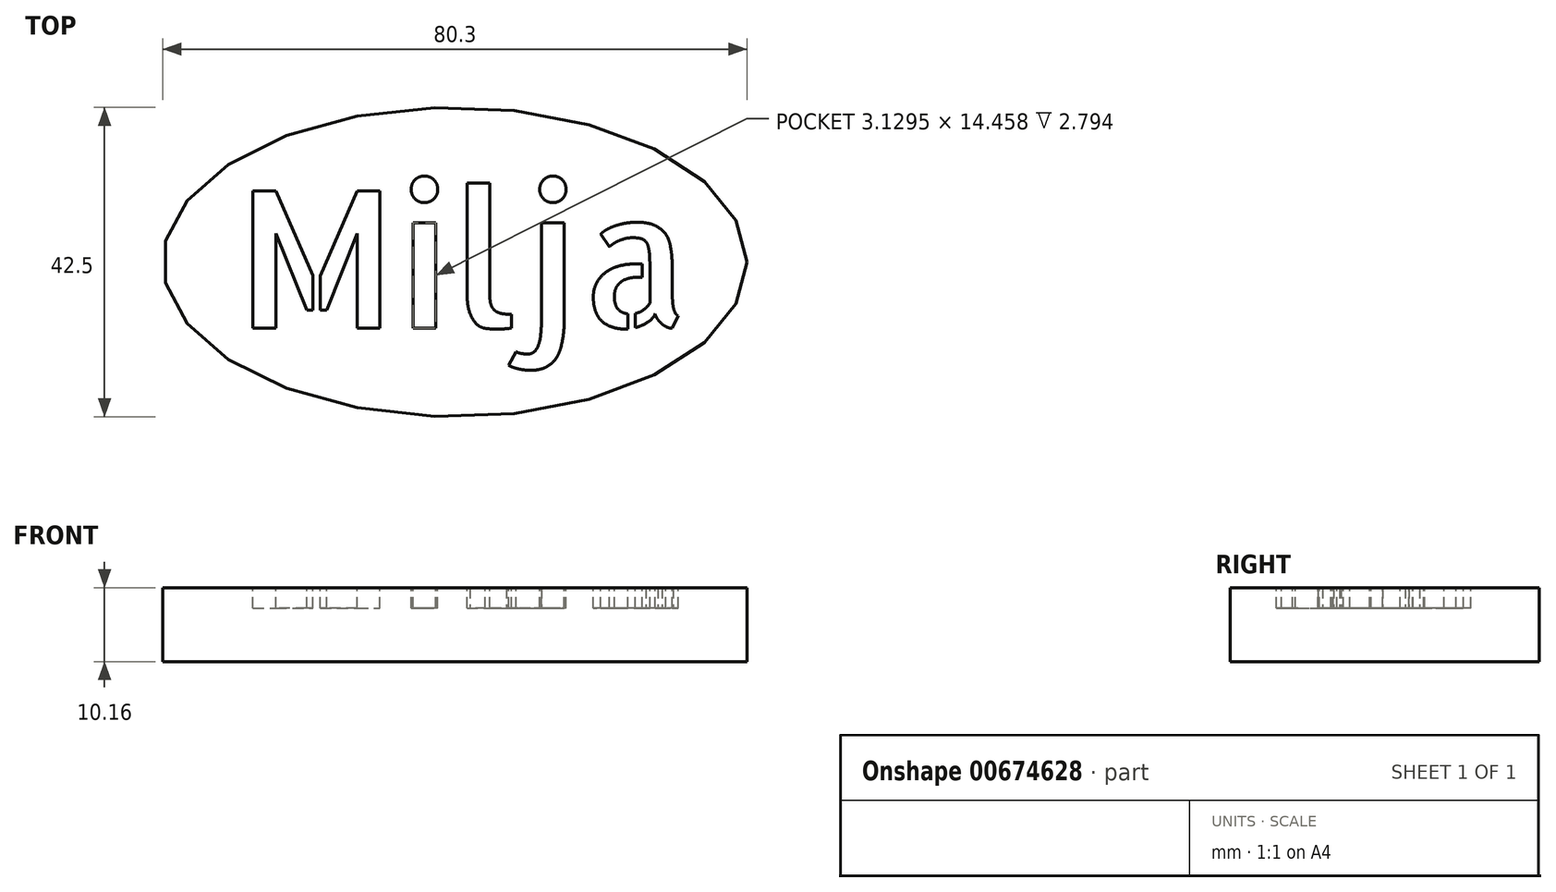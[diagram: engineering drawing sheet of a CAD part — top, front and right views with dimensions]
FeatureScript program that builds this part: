
annotation { "Feature Type Name" : "Feature", "Feature Type Description" : "" }
export const myFeature = defineFeature(function(context is Context, id is Id, definition is map)
    precondition{}
    {
        {
            var Q0;
            Q0=qCreatedBy(makeId("Top.planeOp"),FACE);
            var sketch = newSketch(context, id + "F0", { "sketchPlane" : qUnion([Q0])});
            skEllipse(sketch, "E0", {"center": v(0, 0) * mm, "majorRadius": 40.15 * mm, "minorRadius": 21.25 * mm, "majorAxis": v(1, 0)});
            skSolve(sketch);
        }
        {
            var Q0;
            Q0=makeQuery(id+"F0.imprint","IMPRINT",FACE,{"disambiguationData":[TD([[makeQuery(id+"F0.imprint","IMPRINT",EDGE,{"derivedFrom":sQuery(id+"F0.wireOp",EDGE,"E0")}),1.0]])]});
            extrude(context, id + "F1", {"entities" : qUnion([Q0]), "oppositeDirection" : true, "depth" : 10.16 * mm, "offsetDistance" : 25.4 * mm});
        }
        {
            var Q0;
            Q0=makeQuery(id+"F1.opExtrude","CAP_FACE",FACE,{"disambiguationData":[OSD([sQuery(id+"F0.wireOp",EDGE,"E0")])],"isStart":true});
            var sketch = newSketch(context, id + "F2", { "sketchPlane" : qUnion([Q0])});
            skText(sketch, "E1", { "text": "Milja", "fontName": "AllertaStencil-Regular.ttf"});
            const initialGuessF2  = {"E1": [-0.03011, -0.00909, 1, 0, 0.0189]};
            skSetInitialGuess(sketch, initialGuessF2);
            skSolve(sketch);
        }
        {
            var Q0;
            Q0=makeQuery(id+"F2.imprint","IMPRINT",FACE,{"disambiguationData":[TD([[makeQuery(id+"F2.imprint","IMPRINT",EDGE,{"derivedFrom":sQuery(id+"F2.wireOp",EDGE,"E1.sketch_text.stroke-28")}),-1.0]])]});
            var Q1;
            Q1=makeQuery(id+"F2.imprint","IMPRINT",FACE,{"disambiguationData":[TD([[makeQuery(id+"F2.imprint","IMPRINT",EDGE,{"derivedFrom":sQuery(id+"F2.wireOp",EDGE,"E1.sketch_text.stroke-16")}),-1.0]])]});
            var Q2;
            Q2=makeQuery(id+"F2.imprint","IMPRINT",FACE,{"disambiguationData":[TD([[makeQuery(id+"F2.imprint","IMPRINT",EDGE,{"derivedFrom":sQuery(id+"F2.wireOp",EDGE,"E1.sketch_text.stroke-20")}),-1.0]])]});
            var Q3;
            Q3=makeQuery(id+"F2.imprint","IMPRINT",FACE,{"disambiguationData":[TD([[makeQuery(id+"F2.imprint","IMPRINT",EDGE,{"derivedFrom":sQuery(id+"F2.wireOp",EDGE,"E1.sketch_text.stroke-8")}),-1.0]])]});
            var Q4;
            Q4=makeQuery(id+"F2.imprint","IMPRINT",FACE,{"disambiguationData":[TD([[makeQuery(id+"F2.imprint","IMPRINT",EDGE,{"derivedFrom":sQuery(id+"F2.wireOp",EDGE,"E1.sketch_text.stroke-0")}),-1.0]])]});
            var Q5;
            Q5 = qSketchRegion(id + "F2", true);
            extrude(context, id + "F3", {"entities" : qUnion([Q0, Q1, Q2, Q3, Q4, Q5]), "operationType" : NewBodyOperationType.REMOVE, "oppositeDirection" : true, "depth" : 2.8 * mm, "offsetDistance" : 25.4 * mm});
        }
        {
            var Q0;
            Q0=makeQuery(id+"F1.opExtrude","CAP_FACE",FACE,{"disambiguationData":[OSD([sQuery(id+"F0.wireOp",EDGE,"E0")])],"isStart":true});
            var sketch = newSketch(context, id + "F4", { "sketchPlane" : qUnion([Q0])});
            skEllipse(sketch, "E2", {"center": v(0, 0) * mm, "majorRadius": 39.05 * mm, "minorRadius": 20.16 * mm, "majorAxis": v(-1, 0)});
            skSolve(sketch);
        }
        {
            var Q0;
            Q0=sQuery(id+"F4.wireOp",EDGE,"E2");
            extrude(context, id + "F5", {"bodyType" : ToolBodyType.SURFACE, "surfaceEntities" : qUnion([Q0]), "depth" : 0.5 * mm, "offsetDistance" : 25.4 * mm});
        }
    });
